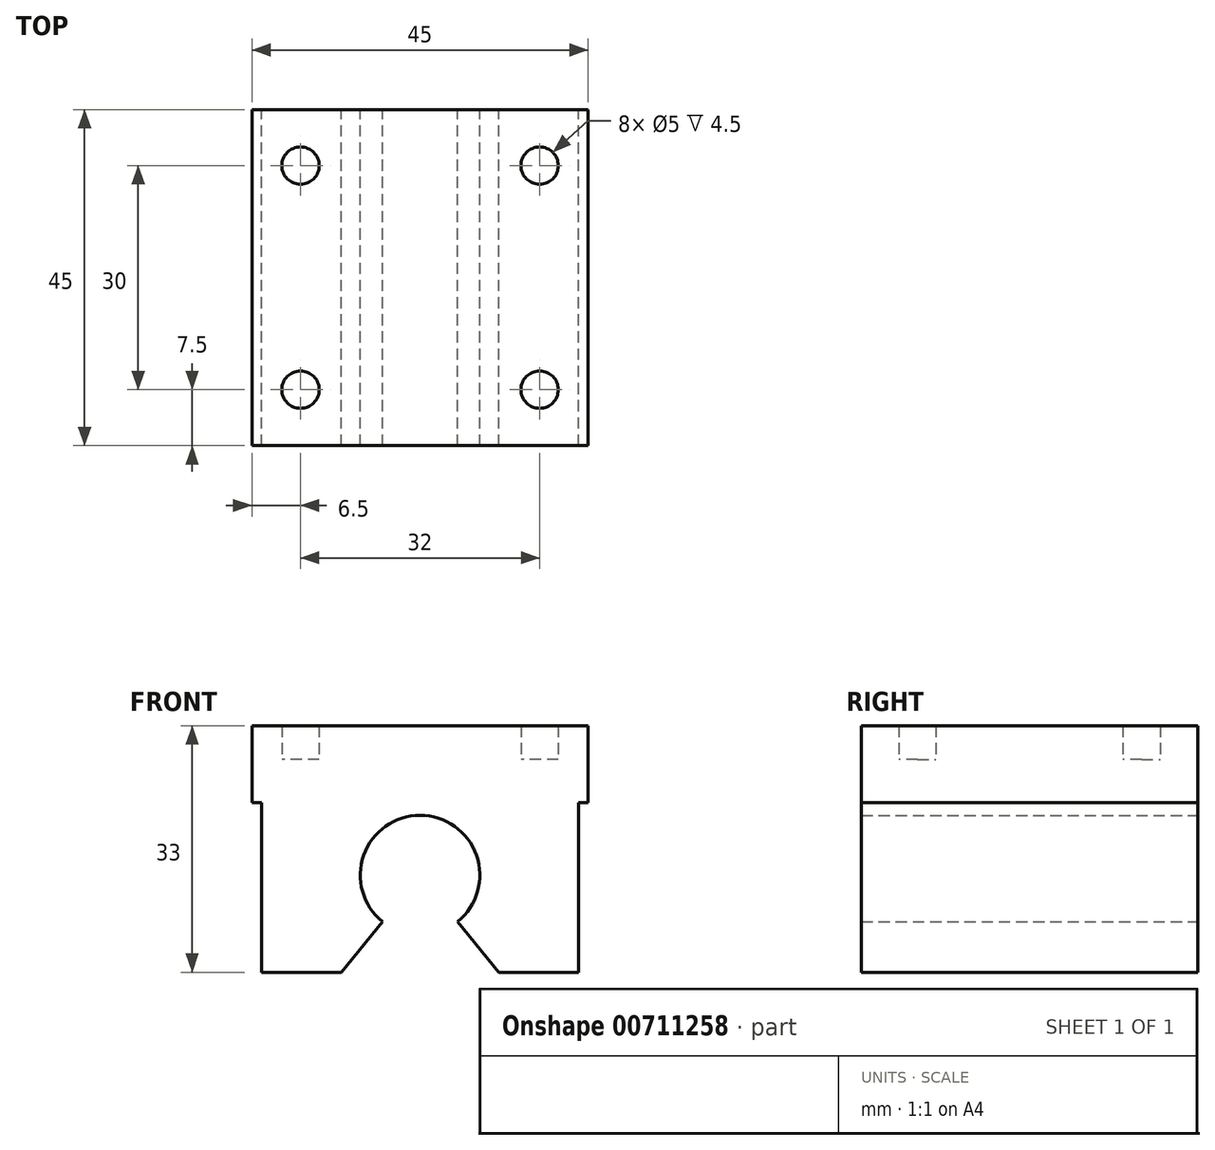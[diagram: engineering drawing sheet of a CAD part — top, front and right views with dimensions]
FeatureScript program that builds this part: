
annotation { "Feature Type Name" : "Feature", "Feature Type Description" : "" }
export const myFeature = defineFeature(function(context is Context, id is Id, definition is map)
    precondition{}
    {
        {
            var Q0;
            Q0=qCreatedBy(makeId("Front.planeOp"),FACE);
            var sketch = newSketch(context, id + "F0", { "sketchPlane" : qUnion([Q0])});
            skLineSegment(sketch, "E0.bottom", {"start": v(22.5, 16.5) * mm, "end": v(-22.5, 16.5) * mm});
            skLineSegment(sketch, "E0.top", {"start": v(22.5, -16.5) * mm, "end": v(-22.5, -16.5) * mm});
            skLineSegment(sketch, "E0.left", {"start": v(22.5, 16.5) * mm, "end": v(22.5, 6.23) * mm});
            skLineSegment(sketch, "E0.right", {"start": v(-22.5, 16.5) * mm, "end": v(-22.5, 6.23) * mm});
            skPoint(sketch, "E0.middle", {"position": v(0, 0) * mm});
            skLineSegment(sketch, "E1.0", {"start": v(-21.23, 6.23) * mm, "end": v(-21.23, -16.5) * mm});
            skLineSegment(sketch, "E2.0", {"start": v(21.23, 6.23) * mm, "end": v(21.23, -16.5) * mm});
            skLineSegment(sketch, "E3.0", {"start": v(22.5, 6.23) * mm, "end": v(21.23, 6.23) * mm});
            skLineSegment(sketch, "E4.trimOffspring", {"start": v(-21.23, 6.23) * mm, "end": v(-22.5, 6.23) * mm});
            skArc(sketch, "E5", {"start": v(5.04, -9.72) * mm, "mid": v(0, 4.5) * mm, "end": v(-5.04, -9.72) * mm});
            skPoint(sketch, "E6.orphan", {"position": v(-21.23, -3.5) * mm});
            skPoint(sketch, "E7.orphan", {"position": v(21.23, -3.5) * mm});
            skLineSegment(sketch, "E8", {"start": v(-5.04, -9.72) * mm, "end": v(-10.53, -16.5) * mm});
            skLineSegment(sketch, "E9", {"start": v(5.04, -9.72) * mm, "end": v(10.53, -16.5) * mm});
            skSolve(sketch);
        }
        {
            var Q0;
            Q0=makeQuery(id+"F0.imprint","IMPRINT",FACE,{"disambiguationData":[TD([[makeQuery(id+"F0.imprint","IMPRINT",EDGE,{"derivedFrom":sQuery(id+"F0.wireOp",EDGE,"E0.bottom")}),1.0]])]});
            extrude(context, id + "F1", {"entities" : qUnion([Q0]), "endBound" : BoundingType.SYMMETRIC, "depth" : 45 * mm, "offsetDistance" : 25 * mm});
        }
        {
            var Q0;
            Q0=qCreatedBy(makeId("Top.planeOp"),FACE);
            var sketch = newSketch(context, id + "F2", { "sketchPlane" : qUnion([Q0])});
            skPoint(sketch, "E10.middle", {"position": v(0, 0) * mm});
            skCircle(sketch, "E11", {"center": v(-16, 15) * mm, "radius": 2.5 * mm});
            skCircle(sketch, "E12", {"center": v(-16, -15) * mm, "radius": 2.5 * mm});
            skCircle(sketch, "E13", {"center": v(16, 15) * mm, "radius": 2.5 * mm});
            skCircle(sketch, "E14", {"center": v(16, -15) * mm, "radius": 2.5 * mm});
            skSolve(sketch);
        }
        {
            var Q0;
            Q0 = qSketchRegion(id + "F2", true);
            extrude(context, id + "F3", {"entities" : qUnion([Q0]), "operationType" : NewBodyOperationType.REMOVE, "oppositeDirection" : true, "depth" : -25 * mm, "offsetDistance" : 25 * mm, "hasSecondDirection" : true, "secondDirectionOppositeDirection" : false, "secondDirectionDepth" : 12 * mm});
        }
    });
